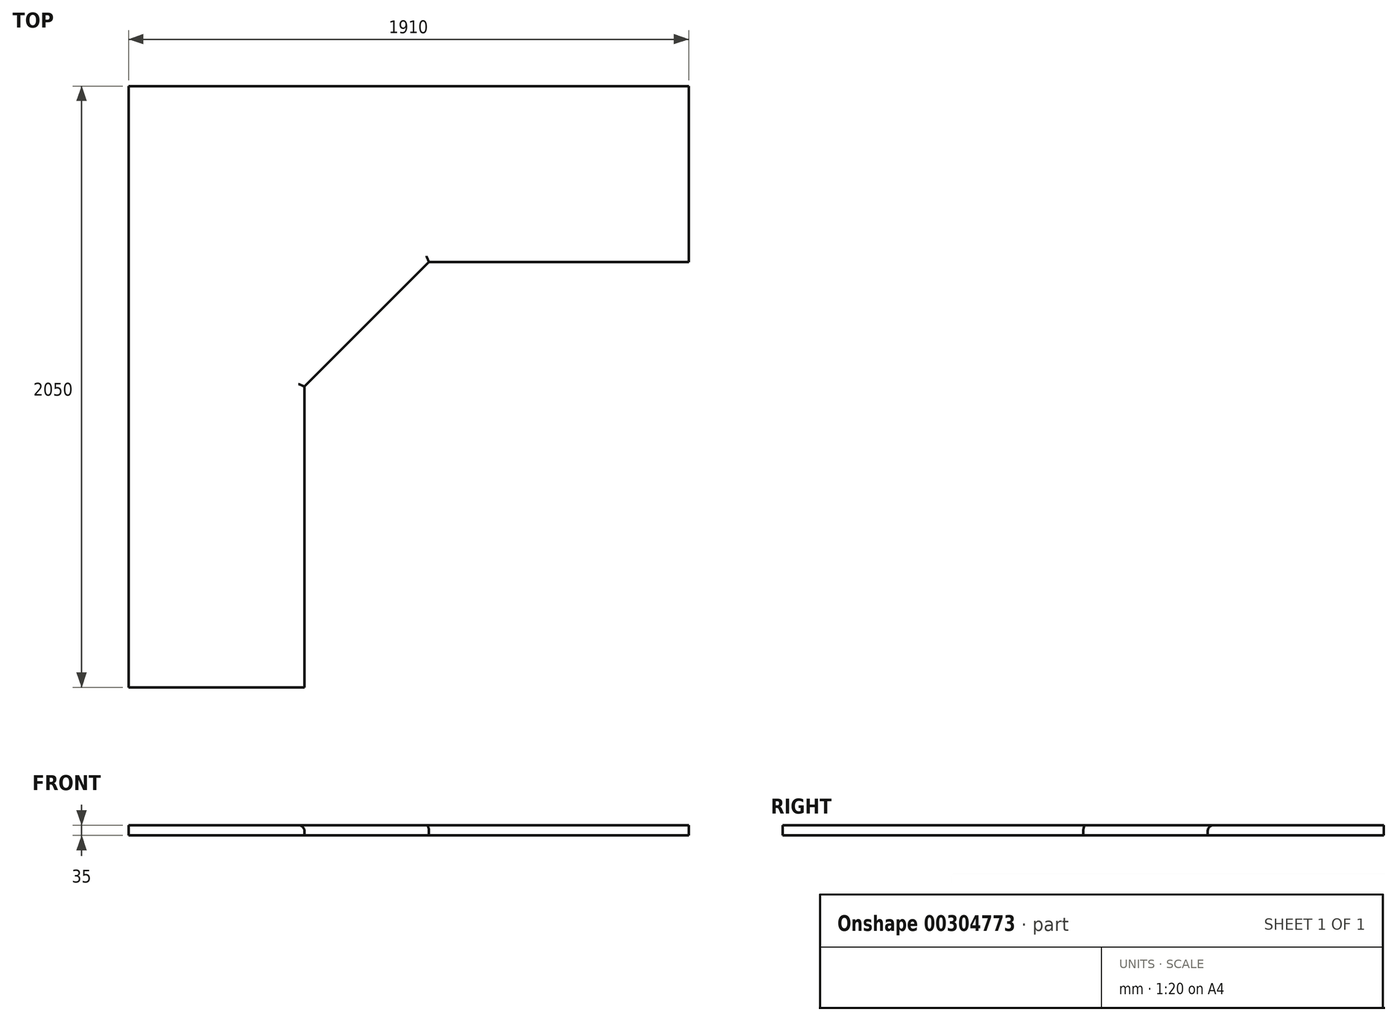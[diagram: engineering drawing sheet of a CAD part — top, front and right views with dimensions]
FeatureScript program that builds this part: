
annotation { "Feature Type Name" : "Feature", "Feature Type Description" : "" }
export const myFeature = defineFeature(function(context is Context, id is Id, definition is map)
    precondition{}
    {
        {
            var Q0;
            Q0=qCreatedBy(makeId("Top.planeOp"),FACE);
            var sketch = newSketch(context, id + "F0", { "sketchPlane" : qUnion([Q0])});
            skLineSegment(sketch, "E0", {"start": v(-993.67, -939.37) * mm, "end": v(-993.67, 1110.63) * mm});
            skLineSegment(sketch, "E1", {"start": v(-993.67, 1110.63) * mm, "end": v(916.33, 1110.63) * mm});
            skLineSegment(sketch, "E2", {"start": v(916.33, 1110.63) * mm, "end": v(916.33, 510.63) * mm});
            skLineSegment(sketch, "E3", {"start": v(916.33, 510.63) * mm, "end": v(30.6, 510.63) * mm});
            skLineSegment(sketch, "E4", {"start": v(30.6, 510.63) * mm, "end": v(-393.67, 86.36) * mm});
            skLineSegment(sketch, "E5", {"start": v(-393.67, 86.36) * mm, "end": v(-393.67, -939.37) * mm});
            skLineSegment(sketch, "E6", {"start": v(-393.67, -939.37) * mm, "end": v(-993.67, -939.37) * mm});
            skSolve(sketch);
        }
        {
            var Q0;
            Q0=makeQuery(id+"F0.imprint","IMPRINT",FACE,{"disambiguationData":[TD([[makeQuery(id+"F0.imprint","IMPRINT",EDGE,{"derivedFrom":sQuery(id+"F0.wireOp",EDGE,"E0")}),-1.0]])]});
            extrude(context, id + "F1", {"entities" : qUnion([Q0]), "offsetDistance" : 25 * mm, "depth" : 35 * mm});
        }
        {
            var Q0;
            Q0=makeQuery(id+"F1.opExtrude","CAP_EDGE",EDGE,{"disambiguationData":[OSD([sQuery(id+"F0.wireOp",EDGE,"E5")])],"isStart":false});
            var Q1;
            Q1=makeQuery(id+"F1.opExtrude","CAP_EDGE",EDGE,{"disambiguationData":[OSD([sQuery(id+"F0.wireOp",EDGE,"E4")])],"isStart":false});
            var Q2;
            Q2=makeQuery(id+"F1.opExtrude","CAP_EDGE",EDGE,{"disambiguationData":[OSD([sQuery(id+"F0.wireOp",EDGE,"E3")])],"isStart":false});
            fillet(context, id + "F2", {"entities" : qUnion([Q0, Q1, Q2]), "radius" : 20 * mm, "tangentPropagation" : true, "allowEdgeOverflow" : false});
        }
    });
